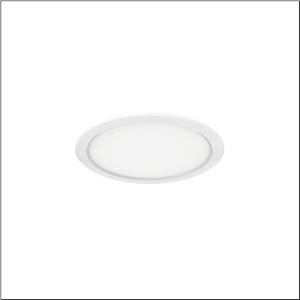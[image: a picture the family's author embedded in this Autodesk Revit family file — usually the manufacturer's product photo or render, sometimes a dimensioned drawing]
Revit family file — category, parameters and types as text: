
# Revit family: lunis_41_eco_51ds107f44a
name_source: partatom
category: Lighting Fixtures
units: mm (PartAtom-declared; Revit-internal decimal feet)

## family parameters
Cut with Voids When Loaded = No
Host = Face
Light Source = No
Part Type = Normal
Room Calculation Point = No
Round Connector Dimension = Use Diameter
Shared = No

## types (1)
- Lunis 41 ECO (1 x LED, 2300 lm, 22 W, 4000K)
    Apparent Load = 22 VA
    CIE Flux Codes = 47 80 97 100 100
    Color Rendering = 80
    Color Temperature = 4000K
    Default Elevation = 1800 mm
    Description = Lunis 41,  ECO, downlight, light emission: direct distribution, LED rated luminous flux: 2.300lm, light colour: 840, control gear: ECG, mains connection: 230V, AC, 50/60Hz, housing, round, of aluminium, coated, traffic white (RAL 9016), diameter: 216mm, recess depth: 58mm, protection rating (complete): IP20, protection rating (on room side): IP40, insulation class (complete): insulation class II (safety insulation), certification: CE, permissible ambient temperature for indoor applications: -20..+40°C, packaging unit: 1 piece
    Height = 0 mm  [stored 0 ft]
    Lamp = 1 x LED
    Lamp Light Flux = 2300 lm
    Lamp Power = 22 W
    Lamp count = 1
    Length = 216 mm
    Luminous efficacy = 105 lm/W
    Manufacturer = Siteco
    ModVariant = No
    Model = 51DS107F44A
    Mounting Place = Ceiling
    Mounting Type = Recessed
    Number of Poles = 1
    OnlyDefault = Yes
    Power Factor = 1
    Product Name = Lunis 41 ECO
    Product group = downlight
    ProductGroupID = 400
    Protection Class = Protection class II
    Protection Degree = IP 20
    RLX_Detail_Level = 1
    RLX_Emergency_Light_Flux = 0 lm
    RLX_Emergency_Type = 0
    RLX_Emergency_Type_DB = No
    RlxData = <blob elided: 22953 chars, md5=007eaa5c>
    Socket = socket
    Standby Power = 0 W
    System Light Flux = 2300 lm
    System Power = 22 W
    Type Comments = Product without accessories
    Type Image = l_1007043.jpg
    URL = http://relux.com
    VarID = ---
    Voltage = 0 V
    Weight = 0.00 kg
    Width = 0 mm  [stored 0 ft]

note: [stored X ft] marks values corroborated as IEEE doubles in the binary element streams (Revit-internal decimal feet)

## geometry (parser evidence)
native form markers: Blend x4, Sweep x12
no freeform markers — native parametric forms only
